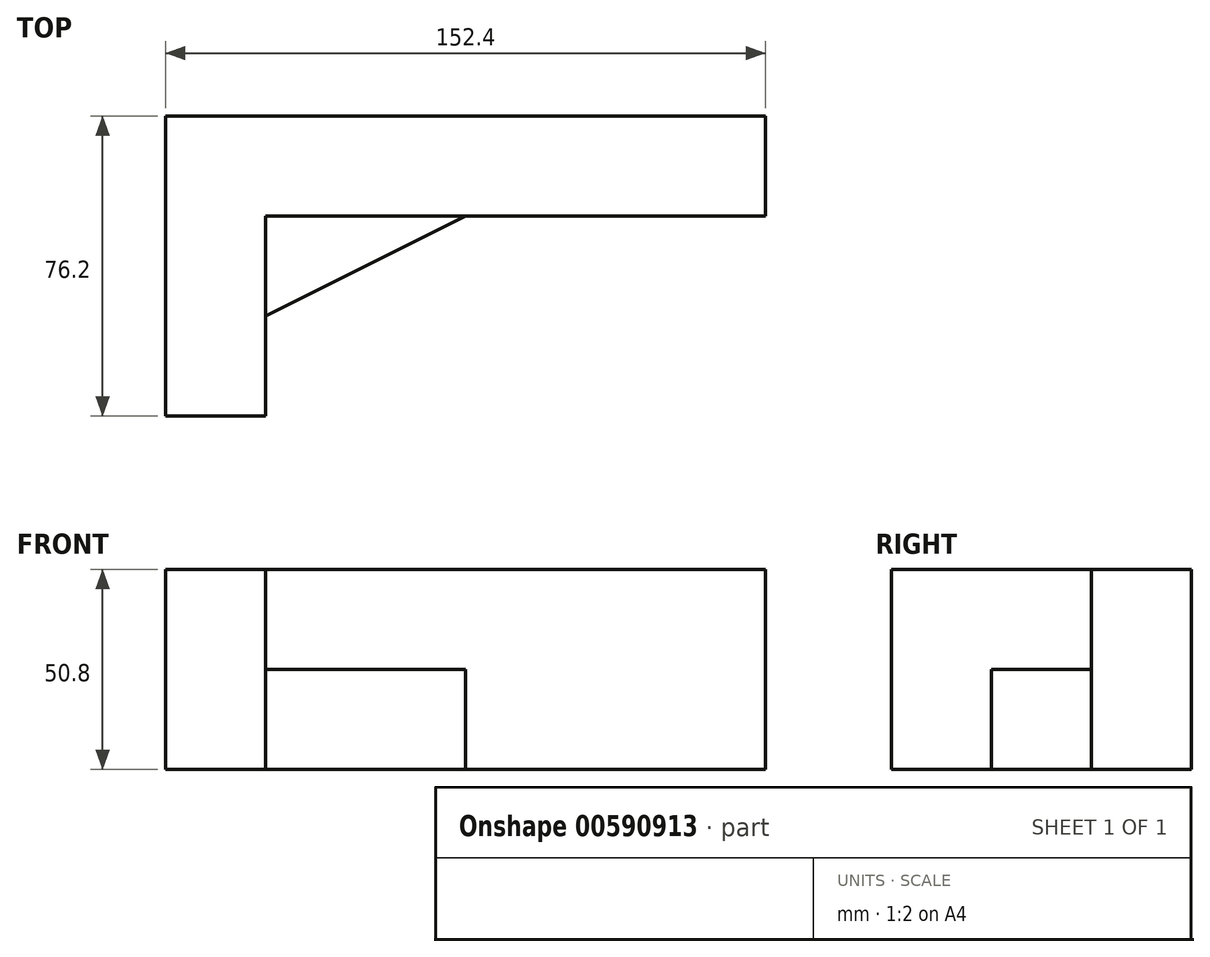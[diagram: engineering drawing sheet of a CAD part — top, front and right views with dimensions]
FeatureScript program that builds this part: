
annotation { "Feature Type Name" : "Feature", "Feature Type Description" : "" }
export const myFeature = defineFeature(function(context is Context, id is Id, definition is map)
    precondition{}
    {
        {
            var Q0;
            Q0=qCreatedBy(makeId("Front.planeOp"),FACE);
            var sketch = newSketch(context, id + "F0", { "sketchPlane" : qUnion([Q0])});
            skLineSegment(sketch, "E0.bottom", {"start": v(0, 0) * mm, "end": v(25.4, 0) * mm});
            skLineSegment(sketch, "E0.top", {"start": v(0, -50.8) * mm, "end": v(25.4, -50.8) * mm});
            skLineSegment(sketch, "E0.left", {"start": v(0, 0) * mm, "end": v(0, -50.8) * mm});
            skLineSegment(sketch, "E0.right", {"start": v(25.4, 0) * mm, "end": v(25.4, -50.8) * mm});
            skSolve(sketch);
        }
        {
            var Q0;
            Q0=makeQuery(id+"F0.imprint","IMPRINT",FACE,{"disambiguationData":[TD([[makeQuery(id+"F0.imprint","IMPRINT",EDGE,{"derivedFrom":sQuery(id+"F0.wireOp",EDGE,"E0.bottom")}),-1.0]])]});
            extrude(context, id + "F1", {"entities" : qUnion([Q0]), "oppositeDirection" : true, "depth" : 76.2 * mm, "offsetDistance" : 25.4 * mm});
        }
        {
            var Q0;
            Q0=makeQuery(id+"F1.opExtrude","SWEPT_FACE",FACE,{"disambiguationData":[OSD([sQuery(id+"F0.wireOp",EDGE,"E0.right")])]});
            var sketch = newSketch(context, id + "F2", { "sketchPlane" : qUnion([Q0])});
            skLineSegment(sketch, "E1", {"start": v(76.2, -50.8) * mm, "end": v(50.8, -50.8) * mm});
            skLineSegment(sketch, "E2", {"start": v(50.8, 0) * mm, "end": v(76.2, 0) * mm});
            skLineSegment(sketch, "E3", {"start": v(76.2, 0) * mm, "end": v(76.2, -50.8) * mm});
            skLineSegment(sketch, "E4", {"start": v(50.8, -50.8) * mm, "end": v(50.8, 0) * mm});
            skSolve(sketch);
        }
        {
            var Q0;
            Q0=makeQuery(id+"F2.imprint","IMPRINT",FACE,{"disambiguationData":[TD([[makeQuery(id+"F2.imprint","IMPRINT",EDGE,{"derivedFrom":sQuery(id+"F2.wireOp",EDGE,"E1")}),-1.0]])]});
            extrude(context, id + "F3", {"entities" : qUnion([Q0]), "operationType" : NewBodyOperationType.ADD, "depth" : 127 * mm, "offsetDistance" : 25.4 * mm});
        }
        {
            var Q0;
            Q0=makeQuery(id+"F3.boolean.opBoolean","MERGE",FACE,{"derivedFrom":[makeQuery(id+"F1.opExtrude","SWEPT_FACE",FACE,{"disambiguationData":[OSD([sQuery(id+"F0.wireOp",EDGE,"E0.top")])]}),makeQuery(id+"F3.opExtrude","SWEPT_FACE",FACE,{"disambiguationData":[OSD([sQuery(id+"F2.wireOp",EDGE,"E1")])]})]});
            var sketch = newSketch(context, id + "F4", { "sketchPlane" : qUnion([Q0])});
            skPoint(sketch, "E5", {"position": v(25.4, -50.8) * mm});
            skLineSegment(sketch, "E6", {"start": v(25.4, -50.8) * mm, "end": v(25.4, -25.4) * mm});
            skLineSegment(sketch, "E7", {"start": v(25.4, -50.8) * mm, "end": v(76.2, -50.8) * mm});
            skLineSegment(sketch, "E8", {"start": v(25.4, -25.4) * mm, "end": v(76.2, -50.8) * mm});
            skSolve(sketch);
        }
        {
            var Q0;
            Q0=makeQuery(id+"F4.imprint","IMPRINT",FACE,{"disambiguationData":[TD([[makeQuery(id+"F4.imprint","IMPRINT",EDGE,{"derivedFrom":sQuery(id+"F4.wireOp",EDGE,"E6")}),-1.0]])]});
            extrude(context, id + "F5", {"entities" : qUnion([Q0]), "operationType" : NewBodyOperationType.ADD, "oppositeDirection" : true, "depth" : 25.4 * mm, "offsetDistance" : 25.4 * mm});
        }
    });
